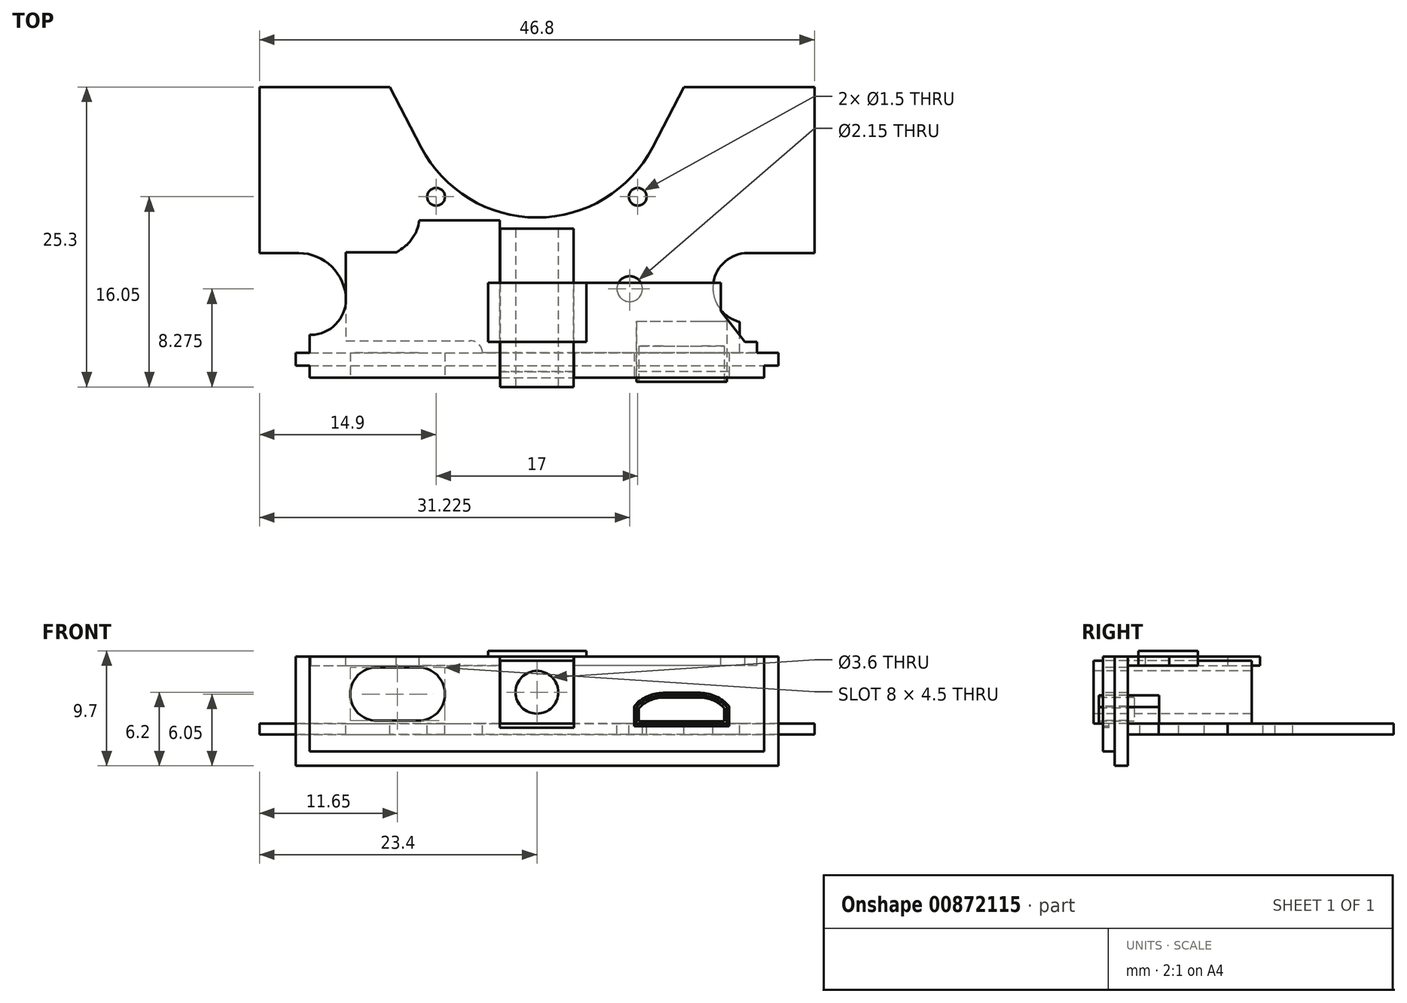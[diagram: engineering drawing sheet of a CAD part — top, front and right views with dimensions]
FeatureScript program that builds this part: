
annotation { "Feature Type Name" : "Feature", "Feature Type Description" : "" }
export const myFeature = defineFeature(function(context is Context, id is Id, definition is map)
    precondition{}
    {
        {
            var Q0;
            Q0=qCreatedBy(makeId("Top.planeOp"),FACE);
            var sketch = newSketch(context, id + "F0", { "sketchPlane" : qUnion([Q0])});
            skLineSegment(sketch, "E0.bottom", {"start": v(-23.4, 12) * mm, "end": v(23.4, 12) * mm});
            skLineSegment(sketch, "E0.top", {"start": v(-23.4, -12) * mm, "end": v(23.4, -12) * mm});
            skLineSegment(sketch, "E0.left", {"start": v(-23.4, 12) * mm, "end": v(-23.4, -12) * mm});
            skLineSegment(sketch, "E0.right", {"start": v(23.4, 12) * mm, "end": v(23.4, -12) * mm});
            skLineSegment(sketch, "E1", {"start": v(-23.4, 12) * mm, "end": v(23.4, -12) * mm, "construction": true});
            skSolve(sketch);
        }
        {
            var Q0;
            Q0 = qSketchRegion(id + "F0", true);
            extrude(context, id + "F1", {"entities" : qUnion([Q0]), "depth" : .9 * mm, "offsetDistance" : 25 * mm});
        }
        {
            var Q0;
            Q0=makeQuery(id+"F1.opExtrude","CAP_FACE",FACE,{"disambiguationData":[OSD([sQuery(id+"F0.wireOp",EDGE,"E0.bottom"),sQuery(id+"F0.wireOp",EDGE,"E0.top"),sQuery(id+"F0.wireOp",EDGE,"E0.left"),sQuery(id+"F0.wireOp",EDGE,"E0.right")])],"isStart":false});
            var sketch = newSketch(context, id + "F2", { "sketchPlane" : qUnion([Q0])});
            skLineSegment(sketch, "E2.bottom", {"start": v(-23.4, -2) * mm, "end": v(-16.1, -2) * mm});
            skLineSegment(sketch, "E2.top", {"start": v(-23.4, -12) * mm, "end": v(-16.1, -12) * mm});
            skLineSegment(sketch, "E2.left", {"start": v(-23.4, -2) * mm, "end": v(-23.4, -12) * mm});
            skLineSegment(sketch, "E2.right", {"start": v(-16.1, -2) * mm, "end": v(-16.1, -9.4) * mm});
            skArc(sketch, "E3", {"start": v(-9.76, 6.92) * mm, "mid": v(0, 1) * mm, "end": v(9.76, 6.92) * mm});
            skLineSegment(sketch, "E4", {"start": v(-4.43, 1) * mm, "end": v(8.5, 1) * mm, "construction": true});
            skLineSegment(sketch, "E5", {"start": v(9.76, 6.92) * mm, "end": v(12.4, 12) * mm});
            skLineSegment(sketch, "E6", {"start": v(-9.76, 6.92) * mm, "end": v(-12.4, 12) * mm});
            skLineSegment(sketch, "E7", {"start": v(-12.4, 12) * mm, "end": v(12.4, 12) * mm});
            skLineSegment(sketch, "E8.bottom", {"start": v(23.4, -12) * mm, "end": v(17.1, -12) * mm});
            skLineSegment(sketch, "E8.top", {"start": v(23.4, -2) * mm, "end": v(17.8, -2) * mm});
            skLineSegment(sketch, "E8.left", {"start": v(23.4, -12) * mm, "end": v(23.4, -2) * mm});
            skLineSegment(sketch, "E8.right", {"start": v(17.1, -12) * mm, "end": v(17.1, -7.8) * mm});
            skArc(sketch, "E9", {"start": v(17.8, -2) * mm, "mid": v(14.87, -4.6) * mm, "end": v(17.1, -7.8) * mm});
            skLineSegment(sketch, "E10", {"start": v(14.85, -2.82) * mm, "end": v(14.85, -7.8) * mm, "construction": true});
            skPoint(sketch, "E11", {"position": v(17.1, -7.8) * mm});
            skLineSegment(sketch, "E12.bottom", {"start": v(-16.1, -9.4) * mm, "end": v(-4.6, -9.4) * mm});
            skLineSegment(sketch, "E12.top", {"start": v(-16.1, -12) * mm, "end": v(-4.6, -12) * mm});
            skLineSegment(sketch, "E12.right", {"start": v(-4.6, -9.4) * mm, "end": v(-4.6, -12) * mm});
            skSolve(sketch);
        }
        {
            var Q0;
            Q0 = qSketchRegion(id + "F2", true);
            extrude(context, id + "F3", {"entities" : qUnion([Q0]), "operationType" : NewBodyOperationType.REMOVE, "oppositeDirection" : true, "depth" : 25 * mm, "offsetDistance" : 25 * mm});
        }
        {
            var Q0;
            Q0=makeQuery(id+"F3.boolean.opBoolean","COPY",EDGE,{"derivedFrom":makeQuery(id+"F3.opExtrude","SWEPT_EDGE",EDGE,{"disambiguationData":[OSD([sQuery(id+"F2.wireOp",EDGE,"E12.bottom"),sQuery(id+"F2.wireOp",EDGE,"E12.right")])]})});
            fillet(context, id + "F4", {"entities" : qUnion([Q0]), "radius" : 1 * mm, "tangentPropagation" : true, "allowEdgeOverflow" : false});
        }
        {
            var Q0;
            Q0=makeQuery(id+"F3.boolean.opBoolean","COPY",EDGE,{"derivedFrom":makeQuery(id+"F3.opExtrude","SWEPT_EDGE",EDGE,{"disambiguationData":[OSD([sQuery(id+"F2.wireOp",EDGE,"E2.bottom"),sQuery(id+"F2.wireOp",EDGE,"E2.right")])]})});
            fillet(context, id + "F5", {"entities" : qUnion([Q0]), "radius" : 4 * mm, "tangentPropagation" : true, "allowEdgeOverflow" : false});
        }
        {
            var Q0;
            Q0=makeQuery(id+"F1.opExtrude","CAP_FACE",FACE,{"disambiguationData":[OSD([sQuery(id+"F0.wireOp",EDGE,"E0.bottom"),sQuery(id+"F0.wireOp",EDGE,"E0.top"),sQuery(id+"F0.wireOp",EDGE,"E0.left"),sQuery(id+"F0.wireOp",EDGE,"E0.right")])],"isStart":false});
            var sketch = newSketch(context, id + "F6", { "sketchPlane" : qUnion([Q0])});
            skCircle(sketch, "E13", {"center": v(-8.5, 2.75) * mm, "radius": 0.75 * mm});
            skCircle(sketch, "E14", {"center": v(8.5, 2.75) * mm, "radius": 0.75 * mm});
            skLineSegment(sketch, "E15", {"start": v(-7.75, 4) * mm, "end": v(-7.75, 0) * mm, "construction": true});
            skLineSegment(sketch, "E16", {"start": v(7.75, 3.53) * mm, "end": v(7.75, -0.58) * mm, "construction": true});
            skLineSegment(sketch, "E17", {"start": v(-8.5, 2.75) * mm, "end": v(8.5, 2.75) * mm, "construction": true});
            skPoint(sketch, "E18", {"position": v(0, 2.75) * mm});
            skLineSegment(sketch, "E19", {"start": v(6.49, 2) * mm, "end": v(11.75, 2) * mm, "construction": true});
            skSolve(sketch);
        }
        {
            var Q0;
            Q0 = qSketchRegion(id + "F6", true);
            extrude(context, id + "F7", {"entities" : qUnion([Q0]), "operationType" : NewBodyOperationType.REMOVE, "oppositeDirection" : true, "depth" : 25 * mm, "offsetDistance" : 25 * mm});
        }
        {
            var Q0;
            Q0=makeQuery(id+"F1.opExtrude","CAP_FACE",FACE,{"disambiguationData":[OSD([sQuery(id+"F0.wireOp",EDGE,"E0.bottom"),sQuery(id+"F0.wireOp",EDGE,"E0.top"),sQuery(id+"F0.wireOp",EDGE,"E0.left"),sQuery(id+"F0.wireOp",EDGE,"E0.right")])],"isStart":false});
            var sketch = newSketch(context, id + "F8", { "sketchPlane" : qUnion([Q0])});
            skCircle(sketch, "E20", {"center": v(7.82, -5.02) * mm, "radius": 1.07 * mm});
            skLineSegment(sketch, "E21", {"start": v(4.15, -6.1) * mm, "end": v(9.67, -6.1) * mm, "construction": true});
            skLineSegment(sketch, "E22", {"start": v(8.9, -2.75) * mm, "end": v(8.9, -9.12) * mm, "construction": true});
            skSolve(sketch);
        }
        {
            var Q0;
            Q0 = qSketchRegion(id + "F8", true);
            extrude(context, id + "F9", {"entities" : qUnion([Q0]), "operationType" : NewBodyOperationType.REMOVE, "oppositeDirection" : true, "depth" : 25 * mm, "offsetDistance" : 25 * mm});
        }
        {
            var Q0;
            Q0=makeQuery(id+"F1.opExtrude","CAP_FACE",FACE,{"disambiguationData":[OSD([sQuery(id+"F0.wireOp",EDGE,"E0.bottom"),sQuery(id+"F0.wireOp",EDGE,"E0.top"),sQuery(id+"F0.wireOp",EDGE,"E0.left"),sQuery(id+"F0.wireOp",EDGE,"E0.right")])],"isStart":false});
            var sketch = newSketch(context, id + "F10", { "sketchPlane" : qUnion([Q0])});
            skLineSegment(sketch, "E23.bottom", {"start": v(8.4, -7.75) * mm, "end": v(16, -7.75) * mm});
            skLineSegment(sketch, "E23.top", {"start": v(8.4, -12.85) * mm, "end": v(16, -12.85) * mm});
            skLineSegment(sketch, "E23.left", {"start": v(8.4, -7.75) * mm, "end": v(8.4, -12.85) * mm});
            skLineSegment(sketch, "E23.right", {"start": v(16, -7.75) * mm, "end": v(16, -12.85) * mm});
            skSolve(sketch);
        }
        {
            var Q0;
            Q0 = qSketchRegion(id + "F10", true);
            extrude(context, id + "F11", {"entities" : qUnion([Q0]), "depth" : 2.4 * mm, "offsetDistance" : 25 * mm});
        }
        {
            var Q0;
            Q0=makeQuery(id+"F11.opExtrude","CAP_EDGE",EDGE,{"disambiguationData":[OSD([sQuery(id+"F10.wireOp",EDGE,"E23.left")])],"isStart":false});
            var Q1;
            Q1=makeQuery(id+"F11.opExtrude","CAP_EDGE",EDGE,{"disambiguationData":[OSD([sQuery(id+"F10.wireOp",EDGE,"E23.right")])],"isStart":false});
            chamfer(context, id + "F12", {"entities" : qUnion([Q0, Q1]), "width" : 1 * mm, "tangentPropagation" : true});
        }
        {
            var Q0;
            {var subQ0=sQuery(id+"F10.wireOp",EDGE,"E23.left");Q0=makeQuery(id+"F12.opChamfer","BLEND_EDGE",EDGE,{"blendedFrom":[makeQuery(id+"F11.opExtrude","CAP_EDGE",EDGE,{"disambiguationData":[OSD([subQ0])],"isStart":false}),makeQuery(id+"F11.opExtrude","CAP_FACE",FACE,{"disambiguationData":[OSD([sQuery(id+"F10.wireOp",EDGE,"E23.bottom"),sQuery(id+"F10.wireOp",EDGE,"E23.top"),subQ0,sQuery(id+"F10.wireOp",EDGE,"E23.right")])],"isStart":false})],"blendedInto":[makeQuery(id+"F11.opExtrude","CAP_FACE",FACE,{"disambiguationData":[OSD([sQuery(id+"F10.wireOp",EDGE,"E23.bottom"),sQuery(id+"F10.wireOp",EDGE,"E23.top"),subQ0,sQuery(id+"F10.wireOp",EDGE,"E23.right")])],"isStart":false})]});}
            var Q1;
            {var subQ0=sQuery(id+"F10.wireOp",EDGE,"E23.right");Q1=makeQuery(id+"F12.opChamfer","BLEND_EDGE",EDGE,{"blendedFrom":[makeQuery(id+"F11.opExtrude","CAP_EDGE",EDGE,{"disambiguationData":[OSD([subQ0])],"isStart":false}),makeQuery(id+"F11.opExtrude","CAP_FACE",FACE,{"disambiguationData":[OSD([sQuery(id+"F10.wireOp",EDGE,"E23.bottom"),sQuery(id+"F10.wireOp",EDGE,"E23.top"),sQuery(id+"F10.wireOp",EDGE,"E23.left"),subQ0])],"isStart":false})],"blendedInto":[makeQuery(id+"F11.opExtrude","CAP_FACE",FACE,{"disambiguationData":[OSD([sQuery(id+"F10.wireOp",EDGE,"E23.bottom"),sQuery(id+"F10.wireOp",EDGE,"E23.top"),sQuery(id+"F10.wireOp",EDGE,"E23.left"),subQ0])],"isStart":false})]});}
            fillet(context, id + "F13", {"entities" : qUnion([Q0, Q1]), "radius" : 3 * mm, "tangentPropagation" : true, "allowEdgeOverflow" : false});
        }
        {
            var Q0;
            Q0=makeQuery(id+"F11.opExtrude","SWEPT_FACE",FACE,{"disambiguationData":[OSD([sQuery(id+"F10.wireOp",EDGE,"E23.top")])]});
            var sketch = newSketch(context, id + "F14", { "sketchPlane" : qUnion([Q0])});
            skArc(sketch, "E24.0", {"start": v(10.64, 3.1) * mm, "mid": v(9.53, 2.87) * mm, "end": v(8.6, 2.22) * mm});
            skLineSegment(sketch, "E24.1", {"start": v(10.64, 3.1) * mm, "end": v(13.76, 3.1) * mm});
            skArc(sketch, "E24.2", {"start": v(15.8, 2.22) * mm, "mid": v(14.87, 2.87) * mm, "end": v(13.76, 3.1) * mm});
            skLineSegment(sketch, "E25.0", {"start": v(8.6, 2.22) * mm, "end": v(8.6, 1.1) * mm});
            skLineSegment(sketch, "E26.0", {"start": v(15.8, 2.22) * mm, "end": v(15.8, 1.1) * mm});
            skLineSegment(sketch, "E27.0", {"start": v(8.6, 1.1) * mm, "end": v(15.8, 1.1) * mm});
            skSolve(sketch);
        }
        {
            var Q0;
            Q0 = qSketchRegion(id + "F14", true);
            extrude(context, id + "F15", {"entities" : qUnion([Q0]), "operationType" : NewBodyOperationType.REMOVE, "oppositeDirection" : true, "depth" : 3 * mm, "offsetDistance" : 25 * mm});
        }
        {
            var Q0;
            Q0=makeQuery(id+"F1.opExtrude","CAP_FACE",FACE,{"disambiguationData":[OSD([sQuery(id+"F0.wireOp",EDGE,"E0.bottom"),sQuery(id+"F0.wireOp",EDGE,"E0.top"),sQuery(id+"F0.wireOp",EDGE,"E0.left"),sQuery(id+"F0.wireOp",EDGE,"E0.right")])],"isStart":false});
            var sketch = newSketch(context, id + "F16", { "sketchPlane" : qUnion([Q0])});
            skLineSegment(sketch, "E28.bottom", {"start": v(-3.1, 0.05) * mm, "end": v(3.1, 0.05) * mm});
            skLineSegment(sketch, "E28.top", {"start": v(-3.1, -14.45) * mm, "end": v(3.1, -14.45) * mm});
            skLineSegment(sketch, "E28.left", {"start": v(-3.1, 0.05) * mm, "end": v(-3.1, -14.45) * mm});
            skLineSegment(sketch, "E28.right", {"start": v(3.1, 0.05) * mm, "end": v(3.1, -14.45) * mm});
            skPoint(sketch, "E29", {"position": v(0, 0.05) * mm});
            skLineSegment(sketch, "E30", {"start": v(0, 0) * mm, "end": v(0, 12.87) * mm, "construction": true});
            skSolve(sketch);
        }
        {
            var Q0;
            Q0 = qSketchRegion(id + "F16", true);
            extrude(context, id + "F17", {"entities" : qUnion([Q0]), "depth" : 5.3 * mm, "offsetDistance" : 25 * mm});
        }
        {
            var Q0;
            Q0=makeQuery(id+"F17.opExtrude","SWEPT_FACE",FACE,{"disambiguationData":[OSD([sQuery(id+"F16.wireOp",EDGE,"E28.top")])]});
            var sketch = newSketch(context, id + "F18", { "sketchPlane" : qUnion([Q0])});
            skCircle(sketch, "E31", {"center": v(0, 3.55) * mm, "radius": 1.8 * mm});
            skLineSegment(sketch, "E32", {"start": v(-3.1, 6.2) * mm, "end": v(3.1, 0.9) * mm, "construction": true});
            skSolve(sketch);
        }
        {
            var Q0;
            Q0 = qSketchRegion(id + "F18", true);
            var Q1;
            Q1=makeQuery(id+"F17.opExtrude","SWEPT_FACE",FACE,{"disambiguationData":[OSD([sQuery(id+"F16.wireOp",EDGE,"E28.bottom")])]});
            extrude(context, id + "F19", {"entities" : qUnion([Q0]), "operationType" : NewBodyOperationType.REMOVE, "endBound" : BoundingType.UP_TO_SURFACE, "oppositeDirection" : true, "depth" : 25 * mm, "endBoundEntityFace" : qUnion([Q1]), "offsetDistance" : 25 * mm});
        }
        {
            var Q0;
            Q0=makeQuery(id+"F17.opExtrude","SWEPT_FACE",FACE,{"disambiguationData":[OSD([sQuery(id+"F16.wireOp",EDGE,"E28.top")])]});
            var sketch = newSketch(context, id + "F20", { "sketchPlane" : qUnion([Q0])});
            skCircle(sketch, "E33", {"center": v(0, 3.55) * mm, "radius": 2.75 * mm});
            skLineSegment(sketch, "E34", {"start": v(-3.1, 6.2) * mm, "end": v(3.1, 0.9) * mm, "construction": true});
            skSolve(sketch);
        }
        {
            var Q0;
            Q0=makeQuery(id+"F20.imprint","IMPRINT",FACE,{"disambiguationData":[TD([[makeQuery(id+"F20.imprint","IMPRINT",EDGE,{"derivedFrom":makeQuery(id+"F19.boolean.opBoolean","COPY",EDGE,{"derivedFrom":makeQuery(id+"F19.opExtrude","CAP_EDGE",EDGE,{"disambiguationData":[OSD([sQuery(id+"F18.wireOp",EDGE,"E31")])],"isStart":true})})}),1.0]])]});
            var Q1;
            {var subQ0=sQuery(id+"F20.wireOp",EDGE,"E33");var subQ1=makeQuery(id+"F17.opExtrude","CAP_EDGE",EDGE,{"disambiguationData":[OSD([sQuery(id+"F16.wireOp",EDGE,"E28.top")])],"isStart":false});var subQ2=makeQuery(id+"F20.imprint","INTERSECT",VERTEX,{"disambiguationData":[OD(0.0)],"derivedFrom":[subQ1,subQ0]});Q1=makeQuery(id+"F20.imprint","IMPRINT",FACE,{"disambiguationData":[TD([[makeQuery(id+"F20.imprint","IMPRINT",EDGE,{"disambiguationData":[TD([[subQ2,1.0]])],"derivedFrom":subQ0}),1.0]])]});}
            var Q2;
            {var subQ0=sQuery(id+"F20.wireOp",EDGE,"E33");var subQ1=makeQuery(id+"F17.opExtrude","CAP_EDGE",EDGE,{"disambiguationData":[OSD([sQuery(id+"F16.wireOp",EDGE,"E28.top")])],"isStart":true});var subQ2=makeQuery(id+"F20.imprint","INTERSECT",VERTEX,{"disambiguationData":[OD(0.0)],"derivedFrom":[subQ1,subQ0]});Q2=makeQuery(id+"F20.imprint","IMPRINT",FACE,{"disambiguationData":[TD([[makeQuery(id+"F20.imprint","IMPRINT",EDGE,{"disambiguationData":[TD([[subQ2,-1.0]])],"derivedFrom":subQ0}),1.0]])]});}
            var Q3;
            {var subQ1=sQuery(id+"F16.wireOp",EDGE,"E28.top");var subQ6=makeQuery(id+"F17.opExtrude","SWEPT_EDGE",EDGE,{"disambiguationData":[OSD([subQ1,sQuery(id+"F16.wireOp",EDGE,"E28.left")])]});Q3=makeQuery(id+"F20.imprint","IMPRINT",FACE,{"disambiguationData":[TD([[makeQuery(id+"F20.imprint","IMPRINT",EDGE,{"derivedFrom":subQ6}),1.0]])]});}
            var Q4;
            {var subQ1=sQuery(id+"F16.wireOp",EDGE,"E28.top");var subQ6=makeQuery(id+"F17.opExtrude","SWEPT_EDGE",EDGE,{"disambiguationData":[OSD([subQ1,sQuery(id+"F16.wireOp",EDGE,"E28.right")])]});Q4=makeQuery(id+"F20.imprint","IMPRINT",FACE,{"disambiguationData":[TD([[makeQuery(id+"F20.imprint","IMPRINT",EDGE,{"derivedFrom":subQ6}),-1.0]])]});}
            extrude(context, id + "F21", {"entities" : qUnion([Q0, Q1, Q2, Q3, Q4]), "operationType" : NewBodyOperationType.REMOVE, "oppositeDirection" : true, "depth" : 1.15 * mm, "offsetDistance" : 25 * mm});
        }
        {
            var Q0;
            {var subQ1=sQuery(id+"F0.wireOp",EDGE,"E0.left");var subQ3=sQuery(id+"F0.wireOp",EDGE,"E0.bottom");Q0=makeQuery(id+"F3.boolean.opBoolean","SPLIT",FACE,{"disambiguationData":[TD([makeQuery(id+"F1.opExtrude","SWEPT_FACE",FACE,{"disambiguationData":[OSD([subQ1])]})])],"derivedFrom":makeQuery(id+"F1.opExtrude","SWEPT_FACE",FACE,{"disambiguationData":[OSD([subQ3])]})});}
            cPlane(context, id + "F22", {"entities" : qUnion([Q0]), "cplaneType" : CPlaneType.OFFSET, "offset" : 24.5 * mm, "oppositeDirection" : true, "width" : 150 * mm, "height" : 150 * mm});
        }
        {
            var Q0;
            Q0=qCreatedBy(id+"F22.planeOp",FACE);
            var sketch = newSketch(context, id + "F23", { "sketchPlane" : qUnion([Q0])});
            skLineSegment(sketch, "E35.bottom", {"start": v(19.15, 6.55) * mm, "end": v(3.12, 6.55) * mm});
            skLineSegment(sketch, "E35.top", {"start": v(19.15, -1.45) * mm, "end": v(-19.15, -1.45) * mm});
            skLineSegment(sketch, "E35.left", {"start": v(19.15, 6.55) * mm, "end": v(19.15, -1.45) * mm});
            skLineSegment(sketch, "E35.right", {"start": v(-19.15, 6.55) * mm, "end": v(-19.15, -1.45) * mm});
            skPoint(sketch, "E36", {"position": v(0, 6.55) * mm});
            skLineSegment(sketch, "E37.top", {"start": v(3.13, 0.55) * mm, "end": v(-3.13, 0.55) * mm});
            skLineSegment(sketch, "E37.left", {"start": v(3.12, 6.55) * mm, "end": v(3.13, 0.55) * mm});
            skLineSegment(sketch, "E37.right", {"start": v(-3.12, 6.55) * mm, "end": v(-3.13, 0.55) * mm});
            skPoint(sketch, "E38", {"position": v(0, 3.55) * mm});
            skLineSegment(sketch, "E39", {"start": v(0, 3.55) * mm, "end": v(-1.1, 3.55) * mm, "construction": true});
            skLineSegment(sketch, "E40.trimOffspring", {"start": v(-3.12, 6.55) * mm, "end": v(-19.15, 6.55) * mm});
            skArc(sketch, "E41.0", {"start": v(-16.2, 2.37) * mm, "mid": v(-15.1, 3.2) * mm, "end": v(-13.76, 3.5) * mm});
            skLineSegment(sketch, "E41.1", {"start": v(-10.64, 3.5) * mm, "end": v(-13.76, 3.5) * mm});
            skArc(sketch, "E41.2", {"start": v(-10.64, 3.5) * mm, "mid": v(-9.3, 3.2) * mm, "end": v(-8.2, 2.37) * mm});
            skLineSegment(sketch, "E42.0", {"start": v(-8.2, 2.37) * mm, "end": v(-8.2, 0.7) * mm});
            skLineSegment(sketch, "E43.0", {"start": v(-16.2, 2.37) * mm, "end": v(-16.2, 0.7) * mm});
            skLineSegment(sketch, "E44.0", {"start": v(-8.2, 0.7) * mm, "end": v(-16.2, 0.7) * mm});
            skSolve(sketch);
        }
        {
            var Q0;
            Q0 = qSketchRegion(id + "F23", true);
            extrude(context, id + "F24", {"entities" : qUnion([Q0]), "depth" : 1 * mm, "offsetDistance" : 25 * mm});
        }
        {
            var Q0;
            Q0=makeQuery(id+"F24.opExtrude","CAP_FACE",FACE,{"disambiguationData":[OSD([sQuery(id+"F23.wireOp",EDGE,"E35.bottom"),sQuery(id+"F23.wireOp",EDGE,"E35.top"),sQuery(id+"F23.wireOp",EDGE,"E35.left"),sQuery(id+"F23.wireOp",EDGE,"E35.right"),sQuery(id+"F23.wireOp",EDGE,"E37.top"),sQuery(id+"F23.wireOp",EDGE,"E37.left"),sQuery(id+"F23.wireOp",EDGE,"E37.right"),sQuery(id+"F23.wireOp",EDGE,"E40.trimOffspring")])],"isStart":false});
            var sketch = newSketch(context, id + "F25", { "sketchPlane" : qUnion([Q0])});
            skLineSegment(sketch, "E45.bottom", {"start": v(20.35, 6.55) * mm, "end": v(3.12, 6.55) * mm});
            skLineSegment(sketch, "E45.top", {"start": v(20.35, -2.65) * mm, "end": v(-20.35, -2.65) * mm});
            skLineSegment(sketch, "E45.left", {"start": v(20.35, 6.55) * mm, "end": v(20.35, -2.65) * mm});
            skLineSegment(sketch, "E45.right", {"start": v(-20.35, 6.55) * mm, "end": v(-20.35, -2.65) * mm});
            skLineSegment(sketch, "E46.0", {"start": v(3.12, 6.55) * mm, "end": v(3.13, 0.55) * mm});
            skLineSegment(sketch, "E46.1", {"start": v(3.13, 0.55) * mm, "end": v(-3.13, 0.55) * mm});
            skLineSegment(sketch, "E46.2", {"start": v(-3.12, 6.55) * mm, "end": v(-3.13, 0.55) * mm});
            skLineSegment(sketch, "E47.trimOffspring", {"start": v(-3.12, 6.55) * mm, "end": v(-20.35, 6.55) * mm});
            skArc(sketch, "E48.0", {"start": v(-10.64, 3.5) * mm, "mid": v(-9.3, 3.2) * mm, "end": v(-8.2, 2.37) * mm});
            skLineSegment(sketch, "E48.1", {"start": v(-10.64, 3.5) * mm, "end": v(-13.76, 3.5) * mm});
            skLineSegment(sketch, "E48.2", {"start": v(-8.2, 2.37) * mm, "end": v(-8.2, 0.7) * mm});
            skLineSegment(sketch, "E48.3", {"start": v(-8.2, 0.7) * mm, "end": v(-16.2, 0.7) * mm});
            skArc(sketch, "E48.4", {"start": v(-16.2, 2.37) * mm, "mid": v(-15.1, 3.2) * mm, "end": v(-13.76, 3.5) * mm});
            skLineSegment(sketch, "E48.5", {"start": v(-16.2, 2.37) * mm, "end": v(-16.2, 0.7) * mm});
            skSolve(sketch);
        }
        {
            var Q0;
            Q0 = qSketchRegion(id + "F25", true);
            extrude(context, id + "F26", {"entities" : qUnion([Q0]), "operationType" : NewBodyOperationType.ADD, "depth" : 1.1 * mm, "offsetDistance" : 25 * mm});
        }
        {
            var Q0;
            Q0=makeQuery(id+"F26.boolean.opBoolean","MERGE",FACE,{"derivedFrom":[makeQuery(id+"F24.opExtrude","SWEPT_FACE",FACE,{"disambiguationData":[OSD([sQuery(id+"F23.wireOp",EDGE,"E35.bottom")])]}),makeQuery(id+"F26.opExtrude","SWEPT_FACE",FACE,{"disambiguationData":[OSD([sQuery(id+"F25.wireOp",EDGE,"E45.bottom")])]})]});
            var sketch = newSketch(context, id + "F27", { "sketchPlane" : qUnion([Q0])});
            skLineSegment(sketch, "E49.bottom", {"start": v(-3.13, -10.4) * mm, "end": v(-19.15, -10.4) * mm});
            skLineSegment(sketch, "E49.top", {"start": v(-3.13, 0.75) * mm, "end": v(-9.93, 0.75) * mm});
            skLineSegment(sketch, "E49.left", {"start": v(-3.13, -10.4) * mm, "end": v(-3.13, 0.75) * mm});
            skLineSegment(sketch, "E50.bottom", {"start": v(-19.15, -10.4) * mm, "end": v(-19.15, -10.4) * mm});
            skLineSegment(sketch, "E50.top", {"start": v(-19.15, -8.9) * mm, "end": v(-19.05, -8.9) * mm});
            skLineSegment(sketch, "E50.left", {"start": v(-19.15, -10.4) * mm, "end": v(-19.15, -8.9) * mm});
            skArc(sketch, "E51", {"start": v(-19.15, -8.9) * mm, "mid": v(-17, -8.04) * mm, "end": v(-16.1, -5.9) * mm});
            skLineSegment(sketch, "E52.trimOffspring", {"start": v(-16.1, -5.9) * mm, "end": v(-16.1, -1.95) * mm});
            skLineSegment(sketch, "E53.top", {"start": v(-16.1, -1.95) * mm, "end": v(-11.85, -1.95) * mm});
            skLineSegment(sketch, "E53.right", {"start": v(-11.85, 0.75) * mm, "end": v(-11.85, -1.95) * mm, "construction": true});
            skFitSpline(sketch, "E54", {"points": [v(-11.85, -1.95) * mm, v(-10.56, -0.82) * mm, v(-9.93, 0.75) * mm], "startDerivative": vector(5.1, 3.3) * mm, "endDerivative": vector(0.45, 4.52) * mm});
            skSolve(sketch);
        }
        {
            var Q0;
            Q0 = qSketchRegion(id + "F27", true);
            extrude(context, id + "F28", {"entities" : qUnion([Q0]), "operationType" : NewBodyOperationType.ADD, "oppositeDirection" : true, "depth" : .75 * mm, "offsetDistance" : 25 * mm});
        }
        {
            var Q0;
            Q0=makeQuery(id+"F28.boolean.opBoolean","MERGE",FACE,{"derivedFrom":[makeQuery(id+"F26.boolean.opBoolean","MERGE",FACE,{"derivedFrom":[makeQuery(id+"F24.opExtrude","SWEPT_FACE",FACE,{"disambiguationData":[OSD([sQuery(id+"F23.wireOp",EDGE,"E35.bottom")])]}),makeQuery(id+"F26.opExtrude","SWEPT_FACE",FACE,{"disambiguationData":[OSD([sQuery(id+"F25.wireOp",EDGE,"E45.bottom")])]})]}),makeQuery(id+"F28.opExtrude","CAP_FACE",FACE,{"disambiguationData":[OSD([sQuery(id+"F27.wireOp",EDGE,"E49.bottom"),sQuery(id+"F27.wireOp",EDGE,"E49.top"),sQuery(id+"F27.wireOp",EDGE,"E49.left"),sQuery(id+"F27.wireOp",EDGE,"E50.top"),sQuery(id+"F27.wireOp",EDGE,"E50.left"),sQuery(id+"F27.wireOp",EDGE,"E51"),sQuery(id+"F27.wireOp",EDGE,"E52.trimOffspring"),sQuery(id+"F27.wireOp",EDGE,"E53.top"),sQuery(id+"F27.wireOp",EDGE,"E54")])],"isStart":true})]});
            var sketch = newSketch(context, id + "F29", { "sketchPlane" : qUnion([Q0])});
            skLineSegment(sketch, "E55.bottom", {"start": v(-4.12, -4.5) * mm, "end": v(4.17, -4.5) * mm});
            skLineSegment(sketch, "E55.top", {"start": v(-4.12, -9.5) * mm, "end": v(4.17, -9.5) * mm});
            skLineSegment(sketch, "E55.left", {"start": v(-4.12, -4.5) * mm, "end": v(-4.12, -9.5) * mm});
            skLineSegment(sketch, "E55.right", {"start": v(4.17, -4.5) * mm, "end": v(4.17, -9.5) * mm});
            skSolve(sketch);
        }
        {
            var Q0;
            Q0 = qSketchRegion(id + "F29", true);
            extrude(context, id + "F30", {"entities" : qUnion([Q0]), "operationType" : NewBodyOperationType.ADD, "depth" : .5 * mm, "offsetDistance" : 25 * mm});
        }
        {
            var Q0;
            Q0=makeQuery(id+"F28.boolean.opBoolean","MERGE",FACE,{"derivedFrom":[makeQuery(id+"F26.boolean.opBoolean","MERGE",FACE,{"derivedFrom":[makeQuery(id+"F24.opExtrude","SWEPT_FACE",FACE,{"disambiguationData":[OSD([sQuery(id+"F23.wireOp",EDGE,"E35.bottom")])]}),makeQuery(id+"F26.opExtrude","SWEPT_FACE",FACE,{"disambiguationData":[OSD([sQuery(id+"F25.wireOp",EDGE,"E45.bottom")])]})]}),makeQuery(id+"F28.opExtrude","CAP_FACE",FACE,{"disambiguationData":[OSD([sQuery(id+"F27.wireOp",EDGE,"E49.bottom"),sQuery(id+"F27.wireOp",EDGE,"E49.top"),sQuery(id+"F27.wireOp",EDGE,"E49.left"),sQuery(id+"F27.wireOp",EDGE,"E50.top"),sQuery(id+"F27.wireOp",EDGE,"E50.left"),sQuery(id+"F27.wireOp",EDGE,"E51"),sQuery(id+"F27.wireOp",EDGE,"E52.trimOffspring"),sQuery(id+"F27.wireOp",EDGE,"E53.top"),sQuery(id+"F27.wireOp",EDGE,"E54")])],"isStart":true})]});
            var sketch = newSketch(context, id + "F31", { "sketchPlane" : qUnion([Q0])});
            skLineSegment(sketch, "E56.bottom", {"start": v(3.1, -4.5) * mm, "end": v(15.5, -4.5) * mm});
            skLineSegment(sketch, "E56.top", {"start": v(3.1, -10.4) * mm, "end": v(15.5, -10.4) * mm});
            skLineSegment(sketch, "E56.left", {"start": v(3.1, -4.5) * mm, "end": v(3.1, -10.4) * mm});
            skLineSegment(sketch, "E56.right", {"start": v(15.5, -4.5) * mm, "end": v(15.5, -6.9) * mm});
            skLineSegment(sketch, "E57", {"start": v(15.5, -6.9) * mm, "end": v(17.55, -9.5) * mm});
            skLineSegment(sketch, "E58", {"start": v(17.55, -9.5) * mm, "end": v(18.55, -9.5) * mm});
            skLineSegment(sketch, "E59", {"start": v(18.55, -9.5) * mm, "end": v(18.55, -10.4) * mm});
            skLineSegment(sketch, "E60", {"start": v(15.5, -10.4) * mm, "end": v(18.55, -10.4) * mm});
            skSolve(sketch);
        }
        {
            var Q0;
            Q0 = qSketchRegion(id + "F31", true);
            var Q1;
            Q1=makeQuery(id+"F28.opExtrude","CAP_FACE",FACE,{"disambiguationData":[OSD([sQuery(id+"F27.wireOp",EDGE,"E49.bottom"),sQuery(id+"F27.wireOp",EDGE,"E49.top"),sQuery(id+"F27.wireOp",EDGE,"E49.left"),sQuery(id+"F27.wireOp",EDGE,"E50.top"),sQuery(id+"F27.wireOp",EDGE,"E50.left"),sQuery(id+"F27.wireOp",EDGE,"E51"),sQuery(id+"F27.wireOp",EDGE,"E52.trimOffspring"),sQuery(id+"F27.wireOp",EDGE,"E53.top"),sQuery(id+"F27.wireOp",EDGE,"E54")])],"isStart":false});
            extrude(context, id + "F32", {"entities" : qUnion([Q0]), "operationType" : NewBodyOperationType.ADD, "endBound" : BoundingType.UP_TO_SURFACE, "oppositeDirection" : true, "depth" : 25 * mm, "endBoundEntityFace" : qUnion([Q1]), "offsetDistance" : 25 * mm});
        }
        {
            var Q0;
            Q0=makeQuery(id+"F24.opExtrude","CAP_FACE",FACE,{"disambiguationData":[OSD([sQuery(id+"F23.wireOp",EDGE,"E35.bottom"),sQuery(id+"F23.wireOp",EDGE,"E35.top"),sQuery(id+"F23.wireOp",EDGE,"E35.left"),sQuery(id+"F23.wireOp",EDGE,"E35.right"),sQuery(id+"F23.wireOp",EDGE,"E37.top"),sQuery(id+"F23.wireOp",EDGE,"E37.left"),sQuery(id+"F23.wireOp",EDGE,"E37.right"),sQuery(id+"F23.wireOp",EDGE,"E40.trimOffspring"),sQuery(id+"F23.wireOp",EDGE,"E41.0"),sQuery(id+"F23.wireOp",EDGE,"E41.1"),sQuery(id+"F23.wireOp",EDGE,"E41.2"),sQuery(id+"F23.wireOp",EDGE,"E42.0"),sQuery(id+"F23.wireOp",EDGE,"E43.0"),sQuery(id+"F23.wireOp",EDGE,"E44.0")])],"isStart":true});
            var sketch = newSketch(context, id + "F33", { "sketchPlane" : qUnion([Q0])});
            skLineSegment(sketch, "E61", {"start": v(-15.75, 3.4) * mm, "end": v(-7.75, 3.4) * mm, "construction": true});
            skArc(sketch, "E62", {"start": v(-13.5, 5.65) * mm, "mid": v(-15.75, 3.4) * mm, "end": v(-13.5, 1.15) * mm});
            skLineSegment(sketch, "E63", {"start": v(-13.5, 5.65) * mm, "end": v(-10, 5.65) * mm});
            skLineSegment(sketch, "E64", {"start": v(-13.5, 1.15) * mm, "end": v(-10, 1.15) * mm});
            skArc(sketch, "E65.trimOffspring", {"start": v(-10, 1.15) * mm, "mid": v(-7.75, 3.4) * mm, "end": v(-10, 5.65) * mm});
            skSolve(sketch);
        }
        {
            var Q0;
            Q0 = qSketchRegion(id + "F33", true);
            extrude(context, id + "F34", {"entities" : qUnion([Q0]), "operationType" : NewBodyOperationType.REMOVE, "oppositeDirection" : true, "depth" : 25 * mm, "offsetDistance" : 25 * mm});
        }
    });
